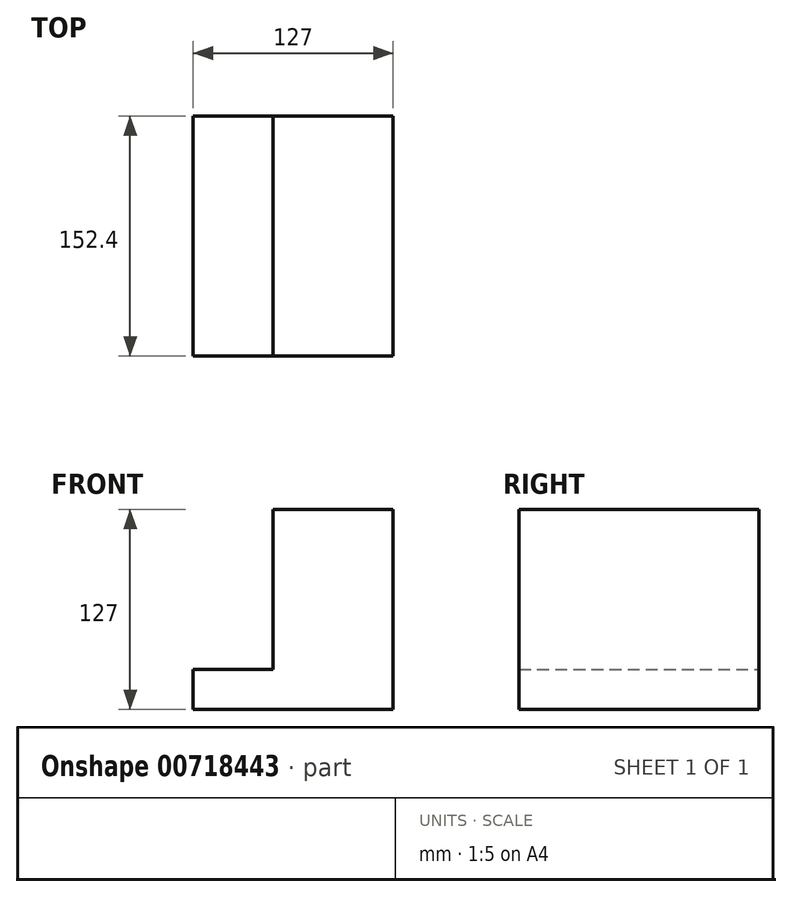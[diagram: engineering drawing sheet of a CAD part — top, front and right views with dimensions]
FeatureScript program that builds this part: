
annotation { "Feature Type Name" : "Feature", "Feature Type Description" : "" }
export const myFeature = defineFeature(function(context is Context, id is Id, definition is map)
    precondition{}
    {
        {
            var Q0;
            Q0=qCreatedBy(makeId("Front.planeOp"),FACE);
            var sketch = newSketch(context, id + "F0", { "sketchPlane" : qUnion([Q0])});
            skLineSegment(sketch, "E0", {"start": v(-118.72, -32.27) * mm, "end": v(8.28, -32.27) * mm});
            skLineSegment(sketch, "E1", {"start": v(8.28, -32.27) * mm, "end": v(8.28, 94.73) * mm});
            skLineSegment(sketch, "E2", {"start": v(8.28, 94.73) * mm, "end": v(-67.92, 94.73) * mm});
            skLineSegment(sketch, "E3", {"start": v(-67.92, 94.73) * mm, "end": v(-67.92, -6.87) * mm});
            skLineSegment(sketch, "E4", {"start": v(-67.92, -6.87) * mm, "end": v(-118.72, -6.87) * mm});
            skLineSegment(sketch, "E5", {"start": v(-118.72, -6.87) * mm, "end": v(-118.72, -32.27) * mm});
            skSolve(sketch);
        }
        {
            var Q0;
            Q0 = qSketchRegion(id + "F0", true);
            extrude(context, id + "F1", {"entities" : qUnion([Q0]), "depth" : 152.4 * mm, "offsetDistance" : 25.4 * mm});
        }
    });
